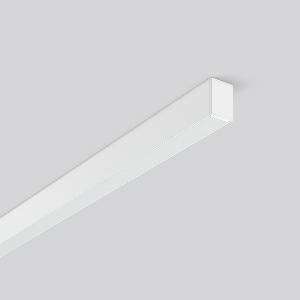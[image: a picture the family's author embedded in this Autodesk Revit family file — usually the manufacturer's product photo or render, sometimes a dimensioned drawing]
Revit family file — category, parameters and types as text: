
# Revit family: less_is_more_27_312196_002_471d
name_source: partatom
category: Lighting Fixtures
units: mm (PartAtom-declared; Revit-internal decimal feet)

## family parameters
Cut with Voids When Loaded = No
Host = Face
Light Source = No
Part Type = Normal
Room Calculation Point = No
Round Connector Dimension = Use Diameter
Shared = No

## types (1)
- LESS IS MORE 27 (1 x LED Modul 830, 1950 lm, 3000)
    Apparent Load = 29 VA
    CIE Flux Codes = 48 79 96 100 100
    Color Rendering = 80
    Color Temperature = 3000
    Default Elevation = 1800 mm
    Description = Series: LESS IS MORE 27
Ceiling and wall luminaire with slim design. Housing: extruded aluminium profile, powder-coated. End cap aluminium powder-coated. Diffuser made of non-yellowing plastic (PMMA), opal. Suitable for Ceiling mounting, Wall (surface). External driver with connecting cable. 
Colour: traffic white, matt (RAL 9016)
Length: 1012 mm
Width: 28 mm
Height: 38 mm
Lamp: LED
Socket: without socket
Colour temperature: 3000K
Colour rendering index (CRI): 82
System power: 29 W
Rated luminous flux: 1950 lm
Luminous efficiency: 67 lm/W
Control gear: Regulated power supply
Protection class: II
Type of protection: IP 20
    Height = 38 mm
    Lamp = 1 x LED Modul 830
    Lamp Light Flux = 1950 lm
    Lamp count = 1
    Length = 1012 mm
    Lifetime = 50000 h
    Luminous efficacy = 67 lm/W
    Manufacturer = RZB
    ModVariant = No
    Model = 312196.002
    Mounting Place = Wall, Ceiling
    Mounting Type = Surface mounted
    Number of Poles = 1
    OnlyDefault = Yes
    Power Factor = 1
    Product Name = LESS IS MORE 27
    Product group = Surface mounted LED linear luminaires
    ProductGroupID = 307
    Protection Class = Protection class II
    Protection Degree = IP 20
    RLX_Detail_Level = 1
    RLX_Emergency_Light_Flux = 0 lm
    RLX_Emergency_Type = 0
    RLX_Emergency_Type_DB = No
    RlxData = <blob elided: 22785 chars, md5=3c121f22>
    Socket = socket
    Standby Power = 0 W
    System Light Flux = 1950 lm
    System Power = 29 W
    Type Comments = Product without accessories
    Type Image = 312196.002.jpg
    URL = http://relux.com
    VarID = ---
    Voltage = 230 V
    Voltage Range = 220-240 V
    Weight = 0.00 kg
    Width = 28 mm

## geometry (parser evidence)
native form markers: Blend x4, Sweep x13
no freeform markers — native parametric forms only
